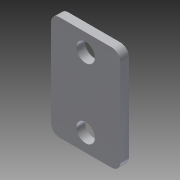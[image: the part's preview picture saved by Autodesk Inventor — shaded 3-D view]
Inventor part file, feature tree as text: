
AUTODESK INVENTOR PART (.ipt)
format: ipt  version: 2013 (Build 170138000, 138)  size: 118,784 bytes
history: native  units: in
note: dims shown in document units (in); Inventor stores cm internally (conversion verified against a paired STEP export)
features: extrude x3, sketch x3, fillet x2
ambient origin geometry x8: Origin, YZ Plane, XZ Plane, XY Plane, X Axis, Y Axis, Z Axis, Center Point
bodies: Solid1 (feature_tree)
feature tree (8):
  extrude  "Extrusion1"  Depth=5.046in
  extrude  "Extrusion2"  Depth=0.5in
  fillet  "Fillet1"  Radius=0.25in
  extrude  "Extrusion3"  Depth=0.266in
  fillet  "Fillet2"  Radius=0.266in
  sketch  "Sketch1"  dims[d0=1.5in d1=5.046in]
  sketch  "Sketch2"  dims[d2=0.125in d3=0.0in d4=0.5in d5=0.25in]
  sketch  "Sketch3"  dims[d6=1.0in d7=0.266in d8=0.266in d9=0.5in d10=0.25in d11=0.266in d12=0.266in d13=1.0in d14=0.125in d15=0.0in d16=0.125in d17=1.0in d18=1.0in d19=0.0in d20=0.125in]
